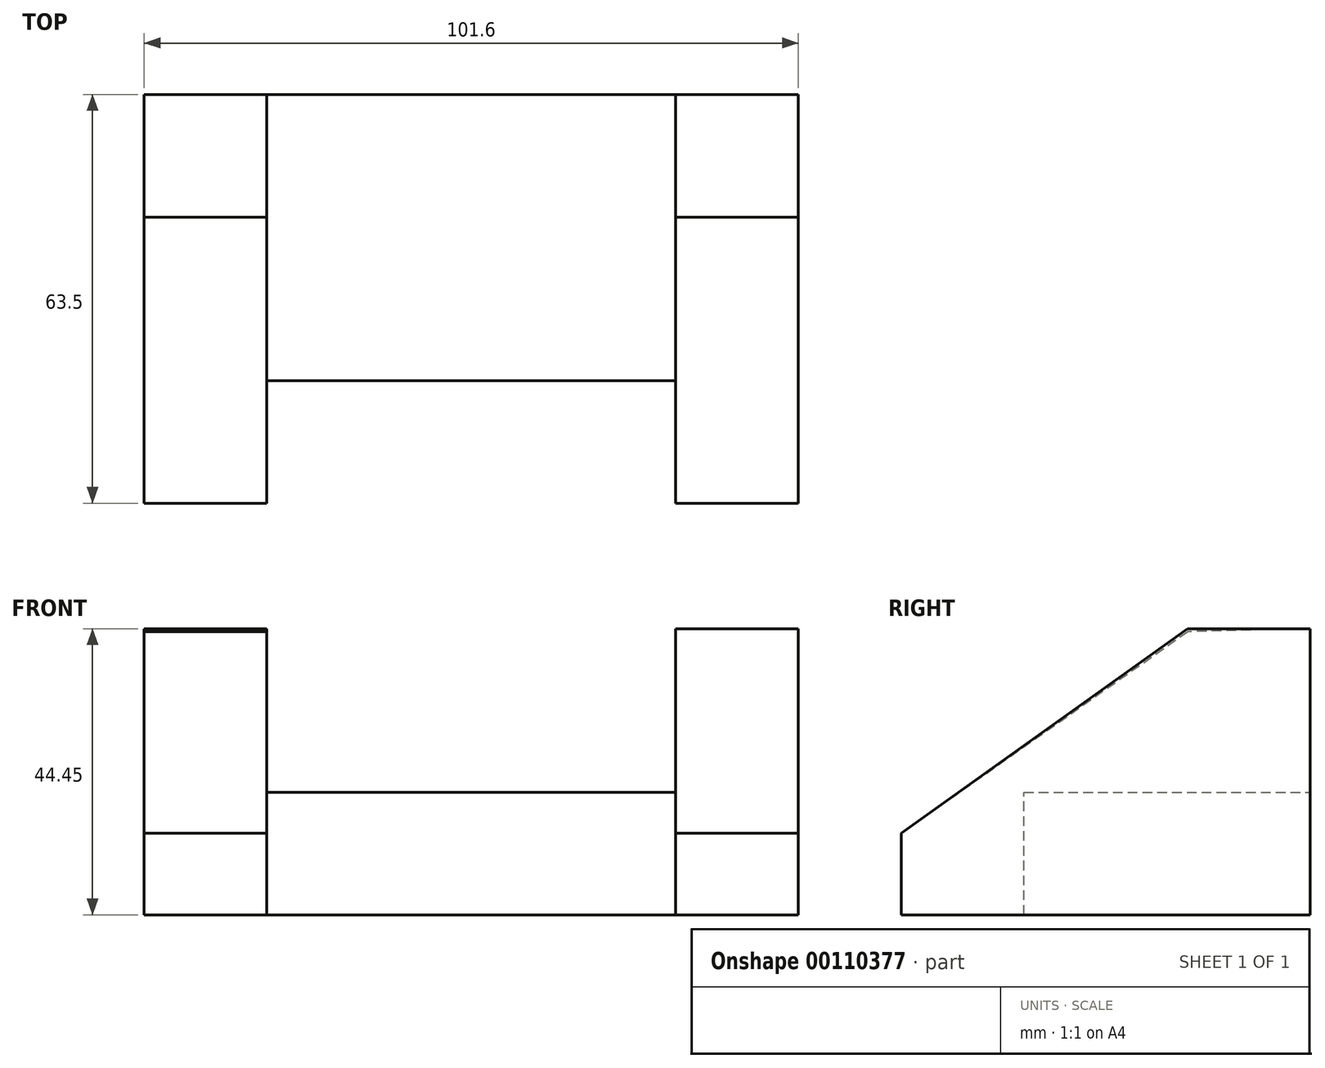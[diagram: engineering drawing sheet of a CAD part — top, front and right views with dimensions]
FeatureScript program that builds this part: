
annotation { "Feature Type Name" : "Feature", "Feature Type Description" : "" }
export const myFeature = defineFeature(function(context is Context, id is Id, definition is map)
    precondition{}
    {
        {
            var Q0;
            Q0=qCreatedBy(makeId("Right.planeOp"),FACE);
            var sketch = newSketch(context, id + "F0", { "sketchPlane" : qUnion([Q0])});
            skLineSegment(sketch, "E0", {"start": v(-44.77, -26.55) * mm, "end": v(-44.77, -13.85) * mm});
            skLineSegment(sketch, "E1", {"start": v(-44.77, -13.85) * mm, "end": v(-0.32, 17.44) * mm});
            skLineSegment(sketch, "E2", {"start": v(18.73, 17.9) * mm, "end": v(18.73, -26.55) * mm});
            skLineSegment(sketch, "E3", {"start": v(18.73, -26.55) * mm, "end": v(-44.77, -26.55) * mm});
            skLineSegment(sketch, "E4", {"start": v(18.73, 17.9) * mm, "end": v(-0.32, 17.44) * mm});
            skSolve(sketch);
        }
        {
            var Q0;
            Q0=makeQuery(id+"F0.imprint","IMPRINT",FACE,{"disambiguationData":[TD([[makeQuery(id+"F0.imprint","IMPRINT",EDGE,{"derivedFrom":sQuery(id+"F0.wireOp",EDGE,"E0")}),-1.0]])]});
            extrude(context, id + "F1", {"entities" : qUnion([Q0]), "oppositeDirection" : true, "depth" : 19.05 * mm});
        }
        {
            var Q0;
            Q0=makeQuery(id+"F1.opExtrude","CAP_FACE",FACE,{"disambiguationData":[OSD([sQuery(id+"F0.wireOp",EDGE,"E0"),sQuery(id+"F0.wireOp",EDGE,"E1"),sQuery(id+"F0.wireOp",EDGE,"E2"),sQuery(id+"F0.wireOp",EDGE,"E3"),sQuery(id+"F0.wireOp",EDGE,"E4")])],"isStart":true});
            var sketch = newSketch(context, id + "F2", { "sketchPlane" : qUnion([Q0])});
            skLineSegment(sketch, "E5", {"start": v(18.73, -7.5) * mm, "end": v(18.73, -26.55) * mm});
            skLineSegment(sketch, "E6", {"start": v(18.73, -26.55) * mm, "end": v(-25.72, -26.55) * mm});
            skLineSegment(sketch, "E7", {"start": v(-25.72, -26.55) * mm, "end": v(-25.72, -7.5) * mm});
            skLineSegment(sketch, "E8", {"start": v(-25.72, -7.5) * mm, "end": v(18.73, -7.5) * mm});
            skSolve(sketch);
        }
        {
            var Q0;
            Q0=makeQuery(id+"F2.imprint","IMPRINT",FACE,{"disambiguationData":[TD([[makeQuery(id+"F2.imprint","IMPRINT",EDGE,{"derivedFrom":sQuery(id+"F2.wireOp",EDGE,"E5")}),-1.0]])]});
            extrude(context, id + "F3", {"entities" : qUnion([Q0]), "operationType" : NewBodyOperationType.ADD, "depth" : 63.5 * mm});
        }
        {
            var Q0;
            Q0=makeQuery(id+"F3.boolean.opBoolean","MERGE",FACE,{"derivedFrom":[makeQuery(id+"F1.opExtrude","SWEPT_FACE",FACE,{"disambiguationData":[OSD([sQuery(id+"F0.wireOp",EDGE,"E3")])]}),makeQuery(id+"F3.opExtrude","SWEPT_FACE",FACE,{"disambiguationData":[OSD([sQuery(id+"F2.wireOp",EDGE,"E6")])]})]});
            var sketch = newSketch(context, id + "F4", { "sketchPlane" : qUnion([Q0])});
            skLineSegment(sketch, "E9", {"start": v(63.5, -18.73) * mm, "end": v(82.55, -18.73) * mm});
            skLineSegment(sketch, "E10", {"start": v(82.55, -18.73) * mm, "end": v(82.55, 44.77) * mm});
            skLineSegment(sketch, "E11", {"start": v(82.55, 44.77) * mm, "end": v(63.5, 44.77) * mm});
            skLineSegment(sketch, "E12", {"start": v(63.5, 44.77) * mm, "end": v(63.5, -18.73) * mm});
            skSolve(sketch);
        }
        {
            var Q0;
            {var subQ5=sQuery(id+"F4.wireOp",EDGE,"E9");Q0=makeQuery(id+"F4.imprint","IMPRINT",FACE,{"disambiguationData":[TD([[makeQuery(id+"F4.imprint","IMPRINT",EDGE,{"derivedFrom":subQ5}),1.0]])]});}
            extrude(context, id + "F5", {"entities" : qUnion([Q0]), "operationType" : NewBodyOperationType.ADD, "oppositeDirection" : true, "depth" : 44.45 * mm});
        }
        {
            var Q0;
            Q0=makeQuery(id+"F5.opExtrude","SWEPT_FACE",FACE,{"disambiguationData":[OSD([sQuery(id+"F4.wireOp",EDGE,"E10")])]});
            var sketch = newSketch(context, id + "F6", { "sketchPlane" : qUnion([Q0])});
            skLineSegment(sketch, "E13", {"start": v(-44.77, -13.85) * mm, "end": v(-0.32, 17.9) * mm});
            skLineSegment(sketch, "E14", {"start": v(-0.32, 17.9) * mm, "end": v(-44.77, 17.9) * mm});
            skLineSegment(sketch, "E15", {"start": v(-44.77, 17.9) * mm, "end": v(-44.77, -13.85) * mm});
            skSolve(sketch);
        }
        {
            var Q0;
            Q0=makeQuery(id+"F6.imprint","IMPRINT",FACE,{"disambiguationData":[TD([[makeQuery(id+"F6.imprint","IMPRINT",EDGE,{"derivedFrom":sQuery(id+"F6.wireOp",EDGE,"E13")}),1.0]])]});
            extrude(context, id + "F7", {"entities" : qUnion([Q0]), "operationType" : NewBodyOperationType.REMOVE, "oppositeDirection" : true, "depth" : 25.4 * mm});
        }
    });
